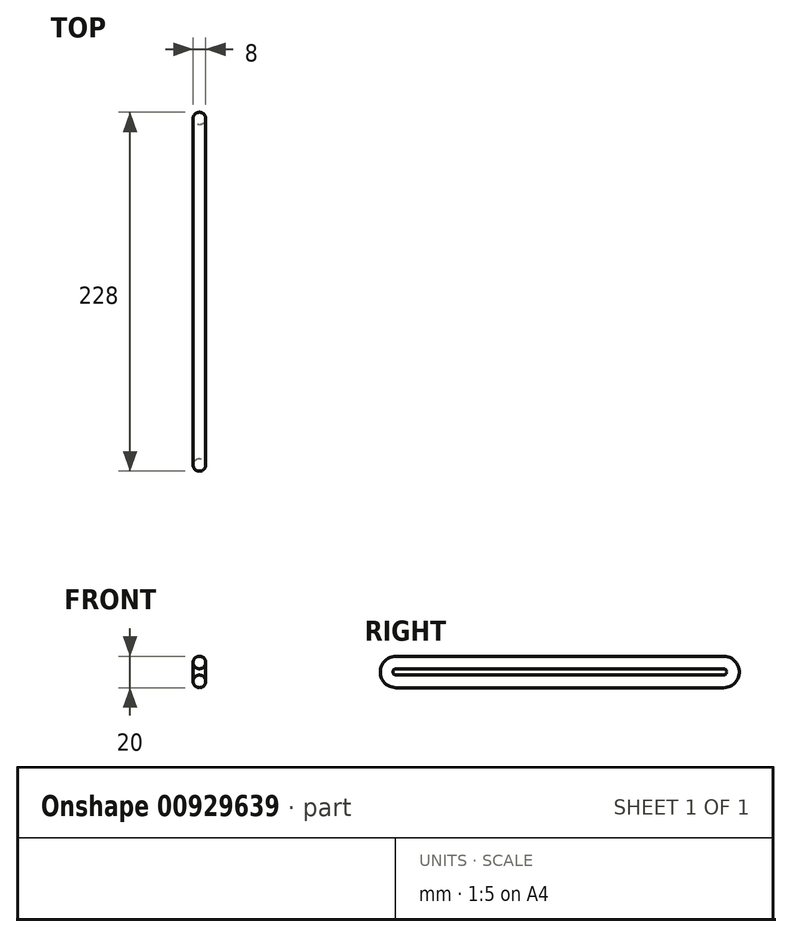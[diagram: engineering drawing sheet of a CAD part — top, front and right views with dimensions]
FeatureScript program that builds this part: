
annotation { "Feature Type Name" : "Feature", "Feature Type Description" : "" }
export const myFeature = defineFeature(function(context is Context, id is Id, definition is map)
    precondition{}
    {
        {
            var Q0;
            Q0=qCreatedBy(makeId("Right.planeOp"),FACE);
            var sketch = newSketch(context, id + "F0", { "sketchPlane" : qUnion([Q0])});
            skLineSegment(sketch, "E0", {"start": v(0, 0) * mm, "end": v(208, 0) * mm});
            skLineSegment(sketch, "E1", {"start": v(0, 12) * mm, "end": v(208, 12) * mm});
            skArc(sketch, "E2", {"start": v(0, 12) * mm, "mid": v(-6, 6) * mm, "end": v(0, 0) * mm});
            skArc(sketch, "E3", {"start": v(208, 12) * mm, "mid": v(214, 6) * mm, "end": v(208, 0) * mm});
            skSolve(sketch);
        }
        {
            var Q0;
            Q0=qCreatedBy(makeId("Front.planeOp"),FACE);
            var sketch = newSketch(context, id + "F1", { "sketchPlane" : qUnion([Q0])});
            skCircle(sketch, "E4", {"center": v(0, 0) * mm, "radius": 4 * mm});
            skSolve(sketch);
        }
        {
            var Q0;
            Q0=makeQuery(id+"F1.imprint","IMPRINT",FACE,{"disambiguationData":[TD([[makeQuery(id+"F1.imprint","IMPRINT",EDGE,{"derivedFrom":sQuery(id+"F1.wireOp",EDGE,"E4")}),1.0]])]});
            var Q1;
            Q1=sQuery(id+"F0.wireOp",EDGE,"E0");
            var Q2;
            Q2=sQuery(id+"F0.wireOp",EDGE,"E1");
            var Q3;
            Q3=sQuery(id+"F0.wireOp",EDGE,"E2");
            var Q4;
            Q4=sQuery(id+"F0.wireOp",EDGE,"E3");
            sweep(context, id + "F2", {"profiles" : qUnion([Q0]), "path" : qUnion([Q1, Q2, Q3, Q4])});
        }
    });
